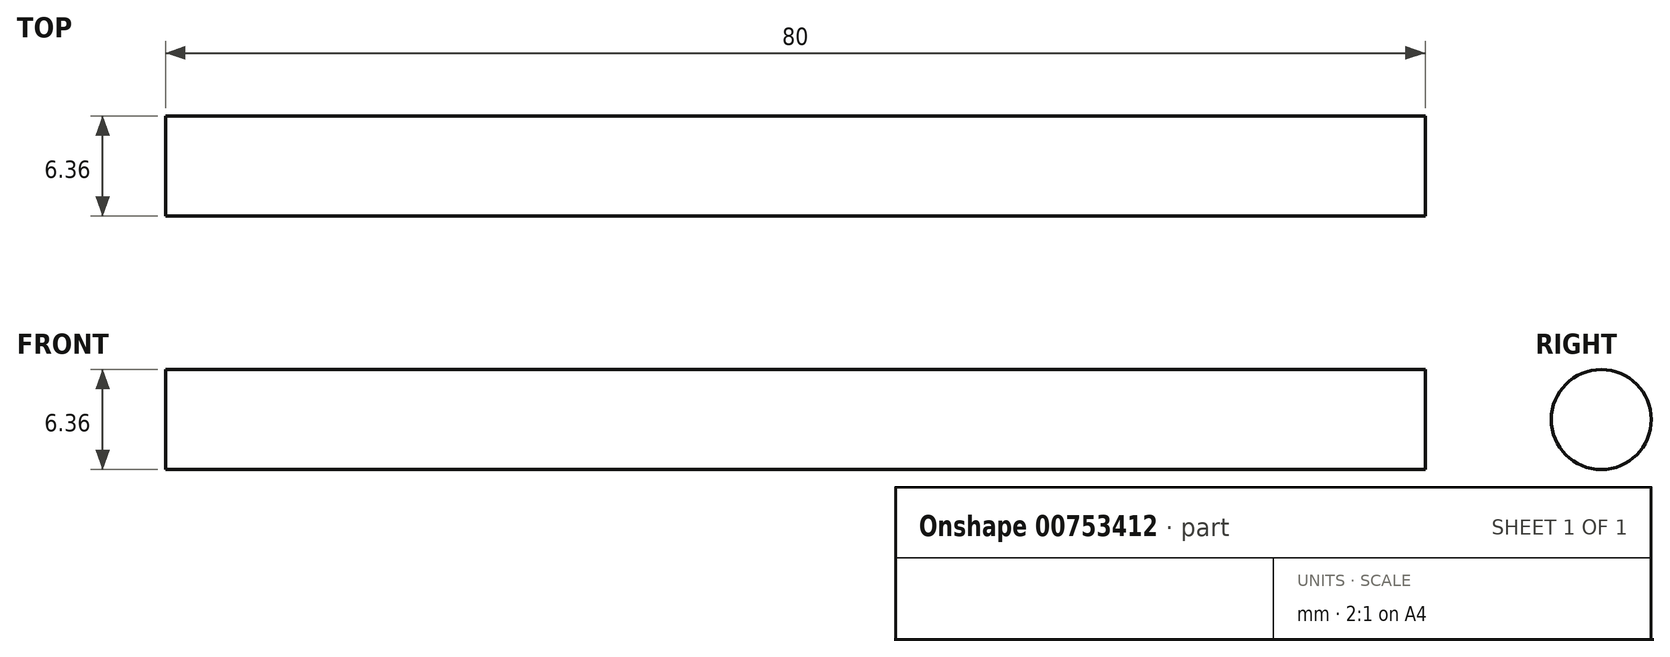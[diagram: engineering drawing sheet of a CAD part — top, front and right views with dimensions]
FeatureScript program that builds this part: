
annotation { "Feature Type Name" : "Feature", "Feature Type Description" : "" }
export const myFeature = defineFeature(function(context is Context, id is Id, definition is map)
    precondition{}
    {
        {
            var Q0;
            Q0=qCreatedBy(makeId("Right.planeOp"),FACE);
            var sketch = newSketch(context, id + "F0", { "sketchPlane" : qUnion([Q0])});
            skCircle(sketch, "E0", {"center": v(0, 0) * mm, "radius": 3.18 * mm});
            skSolve(sketch);
        }
        {
            var Q0;
            Q0=makeQuery(id+"F0.imprint","IMPRINT",FACE,{"disambiguationData":[TD([[makeQuery(id+"F0.imprint","IMPRINT",EDGE,{"derivedFrom":sQuery(id+"F0.wireOp",EDGE,"E0")}),1.0]])]});
            extrude(context, id + "F1", {"entities" : qUnion([Q0]), "depth" : 40 * mm, "offsetDistance" : 25 * mm, "hasSecondDirection" : true, "secondDirectionOppositeDirection" : true, "secondDirectionDepth" : 40 * mm});
        }
    });
